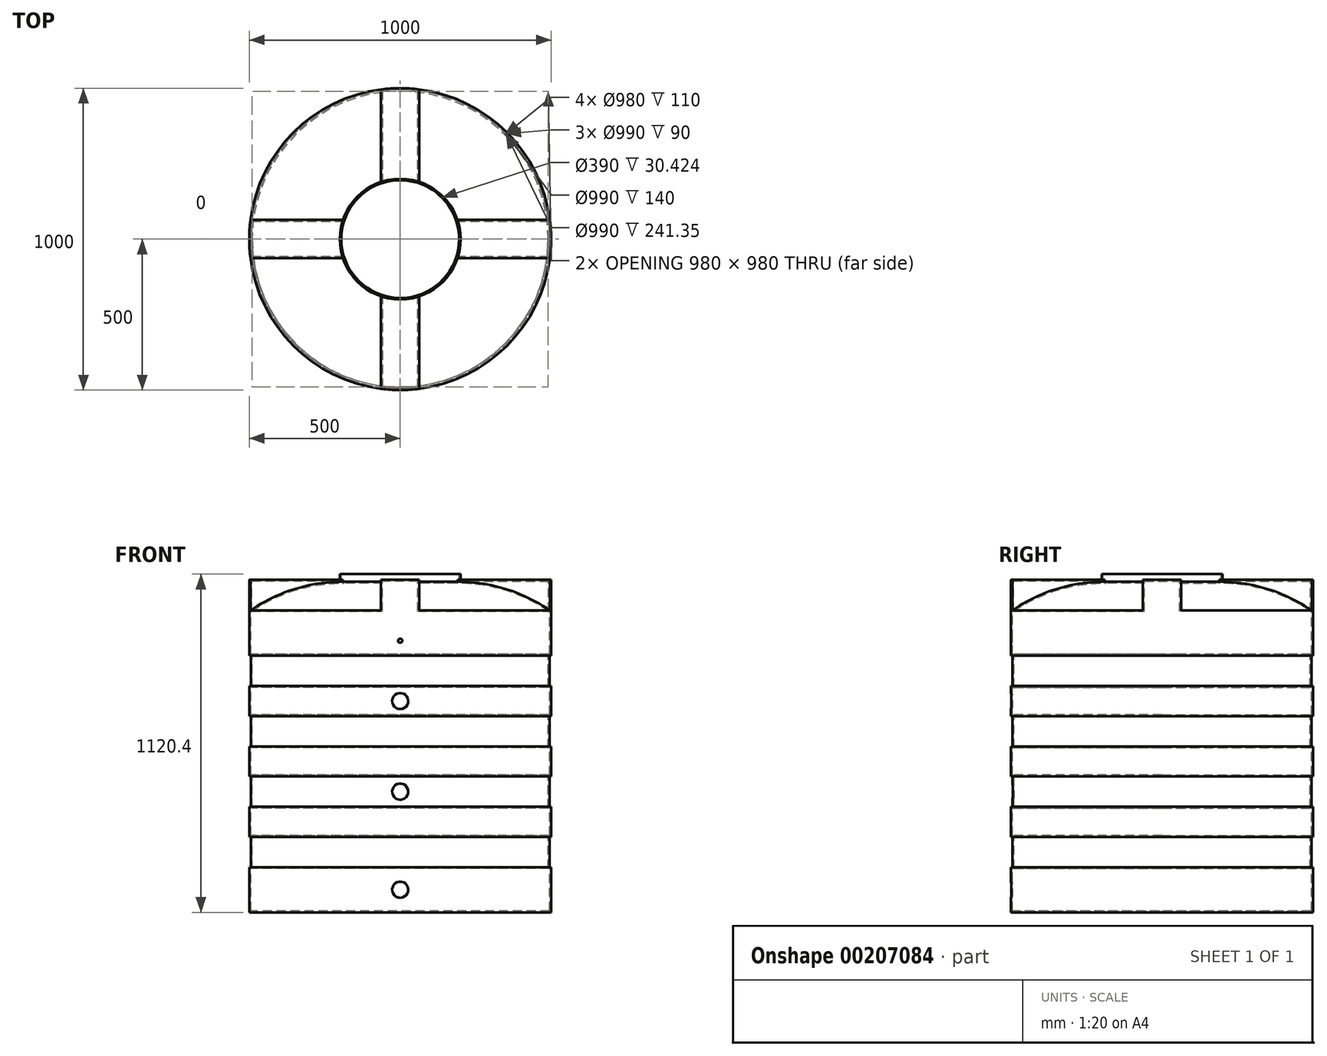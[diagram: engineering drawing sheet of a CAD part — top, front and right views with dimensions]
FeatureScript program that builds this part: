
annotation { "Feature Type Name" : "Feature", "Feature Type Description" : "" }
export const myFeature = defineFeature(function(context is Context, id is Id, definition is map)
    precondition{}
    {
        {
            var Q0;
            Q0=qCreatedBy(makeId("Front.planeOp"),FACE);
            var sketch = newSketch(context, id + "F0", { "sketchPlane" : qUnion([Q0])});
            skLineSegment(sketch, "E0", {"start": v(0, 0) * mm, "end": v(500, 0) * mm});
            skLineSegment(sketch, "E1", {"start": v(200, 1095) * mm, "end": v(200, 1120.4) * mm});
            skLineSegment(sketch, "E2", {"start": v(200, 1120.4) * mm, "end": v(0, 1120.4) * mm});
            skLineSegment(sketch, "E3", {"start": v(0, 1120.4) * mm, "end": v(0, 0) * mm});
            skArc(sketch, "E4", {"start": v(500, 1000) * mm, "mid": v(357.34, 1070.68) * mm, "end": v(200, 1095) * mm});
            skLineSegment(sketch, "E5", {"start": v(500, 1000) * mm, "end": v(-185.76, 1000) * mm, "construction": true});
            skLineSegment(sketch, "E6.bottom", {"start": v(493.65, 1000) * mm, "end": v(200, 1000) * mm});
            skLineSegment(sketch, "E6.top", {"start": v(493.65, 1101.35) * mm, "end": v(200, 1101.35) * mm});
            skLineSegment(sketch, "E6.left", {"start": v(493.65, 1000) * mm, "end": v(493.65, 1101.35) * mm});
            skLineSegment(sketch, "E6.right", {"start": v(200, 1000) * mm, "end": v(200, 1101.35) * mm});
            skLineSegment(sketch, "E7", {"start": v(500, 850) * mm, "end": v(495, 850) * mm});
            skLineSegment(sketch, "E8", {"start": v(495, 850) * mm, "end": v(495, 750) * mm});
            skLineSegment(sketch, "E9", {"start": v(495, 750) * mm, "end": v(500, 750) * mm});
            skLineSegment(sketch, "E10", {"start": v(500, 650) * mm, "end": v(495, 650) * mm});
            skLineSegment(sketch, "E11", {"start": v(495, 650) * mm, "end": v(495, 550) * mm});
            skLineSegment(sketch, "E12", {"start": v(495, 550) * mm, "end": v(500, 550) * mm});
            skLineSegment(sketch, "E13", {"start": v(500, 450) * mm, "end": v(495, 450) * mm});
            skLineSegment(sketch, "E14", {"start": v(495, 450) * mm, "end": v(495, 350) * mm});
            skLineSegment(sketch, "E15", {"start": v(495, 350) * mm, "end": v(500, 350) * mm});
            skLineSegment(sketch, "E16", {"start": v(500, 250) * mm, "end": v(495, 250) * mm});
            skLineSegment(sketch, "E17", {"start": v(495, 250) * mm, "end": v(495, 150) * mm});
            skLineSegment(sketch, "E18", {"start": v(495, 150) * mm, "end": v(500, 150) * mm});
            skLineSegment(sketch, "E19", {"start": v(500, 1000) * mm, "end": v(500, 850) * mm, "construction": true});
            skLineSegment(sketch, "E20", {"start": v(500, 750) * mm, "end": v(500, 650) * mm, "construction": true});
            skLineSegment(sketch, "E21", {"start": v(500, 550) * mm, "end": v(500, 450) * mm});
            skLineSegment(sketch, "E22", {"start": v(500, 350) * mm, "end": v(500, 250) * mm});
            skLineSegment(sketch, "E23", {"start": v(500, 0) * mm, "end": v(500, 150) * mm});
            skLineSegment(sketch, "E24", {"start": v(500, 850) * mm, "end": v(500, 1000) * mm});
            skLineSegment(sketch, "E25", {"start": v(500, 750) * mm, "end": v(500, 650) * mm});
            skSolve(sketch);
        }
        {
            var Q0;
            Q0=makeQuery(id+"F0.imprint","IMPRINT",FACE,{"disambiguationData":[TD([[makeQuery(id+"F0.imprint","IMPRINT",EDGE,{"derivedFrom":sQuery(id+"F0.wireOp",EDGE,"E0")}),1.0]])]});
            var Q1;
            {var subQ0=sQuery(id+"F0.wireOp",EDGE,"E4");Q1=makeQuery(id+"F0.imprint","IMPRINT",FACE,{"disambiguationData":[TD([[makeQuery(id+"F0.imprint","IMPRINT",EDGE,{"derivedFrom":subQ0}),1.0]])]});}
            var Q2;
            Q2=sQuery(id+"F0.wireOp",EDGE,"E3");
            revolve(context, id + "F1", {"entities" : qUnion([Q0, Q1]), "axis" : qUnion([Q2]), "revolveType" : RevolveType.FULL});
        }
        {
            var Q0;
            Q0=makeQuery(id+"F1.opRevolve","SWEPT_FACE",FACE,{"disambiguationData":[OSD([sQuery(id+"F0.wireOp",EDGE,"E2")])]});
            cPlane(context, id + "F2", {"entities" : qUnion([Q0]), "cplaneType" : CPlaneType.OFFSET, "offset" : 19.05 * mm, "oppositeDirection" : true, "width" : 152.4 * mm, "height" : 152.4 * mm});
        }
        {
            var Q0;
            Q0=qCreatedBy(id+"F2.planeOp",FACE);
            var sketch = newSketch(context, id + "F3", { "sketchPlane" : qUnion([Q0])});
            skLineSegment(sketch, "E26", {"start": v(0, 0) * mm, "end": v(785.2, 0) * mm, "construction": true});
            skCircle(sketch, "E27", {"center": v(0, 0) * mm, "radius": 200 * mm, "construction": true});
            skArc(sketch, "E28", {"start": v(200, 0) * mm, "mid": v(197.4, 32.17) * mm, "end": v(189.65, 63.5) * mm});
            skCircle(sketch, "E29", {"center": v(0, 0) * mm, "radius": 500 * mm, "construction": true});
            skArc(sketch, "E30", {"start": v(500, 0) * mm, "mid": v(498.99, 31.81) * mm, "end": v(495.95, 63.5) * mm});
            skLineSegment(sketch, "E31", {"start": v(189.65, 63.5) * mm, "end": v(495.95, 63.5) * mm});
            skLineSegment(sketch, "E32.MirrorCS", {"start": v(189.65, -63.5) * mm, "end": v(495.95, -63.5) * mm});
            skArc(sketch, "E33", {"start": v(200, 0) * mm, "mid": v(197.4, -32.17) * mm, "end": v(189.65, -63.5) * mm});
            skArc(sketch, "E34", {"start": v(500, 0) * mm, "mid": v(498.99, -31.81) * mm, "end": v(495.95, -63.5) * mm});
            skLineSegment(sketch, "E35.1.0", {"start": v(-63.5, 189.65) * mm, "end": v(-63.5, 495.95) * mm});
            skLineSegment(sketch, "E35.1.1", {"start": v(63.5, 189.65) * mm, "end": v(63.5, 495.95) * mm});
            skLineSegment(sketch, "E35.2.0", {"start": v(-189.65, -63.5) * mm, "end": v(-495.95, -63.5) * mm});
            skLineSegment(sketch, "E35.2.1", {"start": v(-189.65, 63.5) * mm, "end": v(-495.95, 63.5) * mm});
            skLineSegment(sketch, "E35.3.0", {"start": v(63.5, -189.65) * mm, "end": v(63.5, -495.95) * mm});
            skLineSegment(sketch, "E35.3.1", {"start": v(-63.5, -189.65) * mm, "end": v(-63.5, -495.95) * mm});
            skArc(sketch, "E36", {"start": v(63.5, 189.65) * mm, "mid": v(0, 200) * mm, "end": v(-63.5, 189.65) * mm});
            skArc(sketch, "E37", {"start": v(63.5, 495.95) * mm, "mid": v(0, 500) * mm, "end": v(-63.5, 495.95) * mm});
            skArc(sketch, "E38", {"start": v(-189.65, 63.5) * mm, "mid": v(-200, 0) * mm, "end": v(-189.65, -63.5) * mm});
            skArc(sketch, "E39", {"start": v(-495.95, 63.5) * mm, "mid": v(-500, 0) * mm, "end": v(-495.95, -63.5) * mm});
            skArc(sketch, "E40", {"start": v(-63.5, -495.95) * mm, "mid": v(0, -500) * mm, "end": v(63.5, -495.95) * mm});
            skArc(sketch, "E41", {"start": v(-63.5, -189.65) * mm, "mid": v(0, -200) * mm, "end": v(63.5, -189.65) * mm});
            skSolve(sketch);
        }
        {
            var Q0;
            Q0 = qSketchRegion(id + "F3", true);
            extrude(context, id + "F4", {"entities" : qUnion([Q0]), "operationType" : NewBodyOperationType.ADD, "oppositeDirection" : true, "depth" : 127 * mm});
        }
        {
            var Q0;
            Q0=makeQuery(id+"F1.opRevolve","SWEPT_FACE",FACE,{"disambiguationData":[OSD([sQuery(id+"F0.wireOp",EDGE,"E2")])]});
            shell(context, id + "F5", {"entities" : qUnion([Q0]), "thickness" : 5 * mm});
        }
        {
            var Q0;
            Q0=qCreatedBy(makeId("Front.planeOp"),FACE);
            cPlane(context, id + "F6", {"entities" : qUnion([Q0]), "cplaneType" : CPlaneType.OFFSET, "offset" : 500 * mm, "width" : 150 * mm, "height" : 150 * mm});
        }
        {
            var Q0;
            Q0=qCreatedBy(id+"F6.planeOp",FACE);
            var sketch = newSketch(context, id + "F7", { "sketchPlane" : qUnion([Q0])});
            skLineSegment(sketch, "E42", {"start": v(0, 0) * mm, "end": v(0, 1146.56) * mm, "construction": true});
            skCircle(sketch, "E43", {"center": v(0, 700) * mm, "radius": 26.67 * mm});
            skLineSegment(sketch, "E44", {"start": v(-604.84, 400) * mm, "end": v(635.7, 400) * mm, "construction": true});
            skLineSegment(sketch, "E45", {"start": v(-608.56, 75) * mm, "end": v(624.55, 75) * mm, "construction": true});
            skCircle(sketch, "E46", {"center": v(0, 400) * mm, "radius": 26.67 * mm});
            skCircle(sketch, "E47", {"center": v(0, 75) * mm, "radius": 26.67 * mm});
            skLineSegment(sketch, "E48", {"start": v(-673.4, 900) * mm, "end": v(815.4, 900) * mm, "construction": true});
            skLineSegment(sketch, "E49", {"start": v(622.16, 700) * mm, "end": v(-658.66, 700) * mm, "construction": true});
            skCircle(sketch, "E50", {"center": v(0, 900) * mm, "radius": 6.99 * mm});
            skSolve(sketch);
        }
        {
            var Q0;
            Q0 = qSketchRegion(id + "F7", true);
            extrude(context, id + "F8", {"entities" : qUnion([Q0]), "operationType" : NewBodyOperationType.REMOVE, "oppositeDirection" : true, "depth" : 25 * mm});
        }
    });
